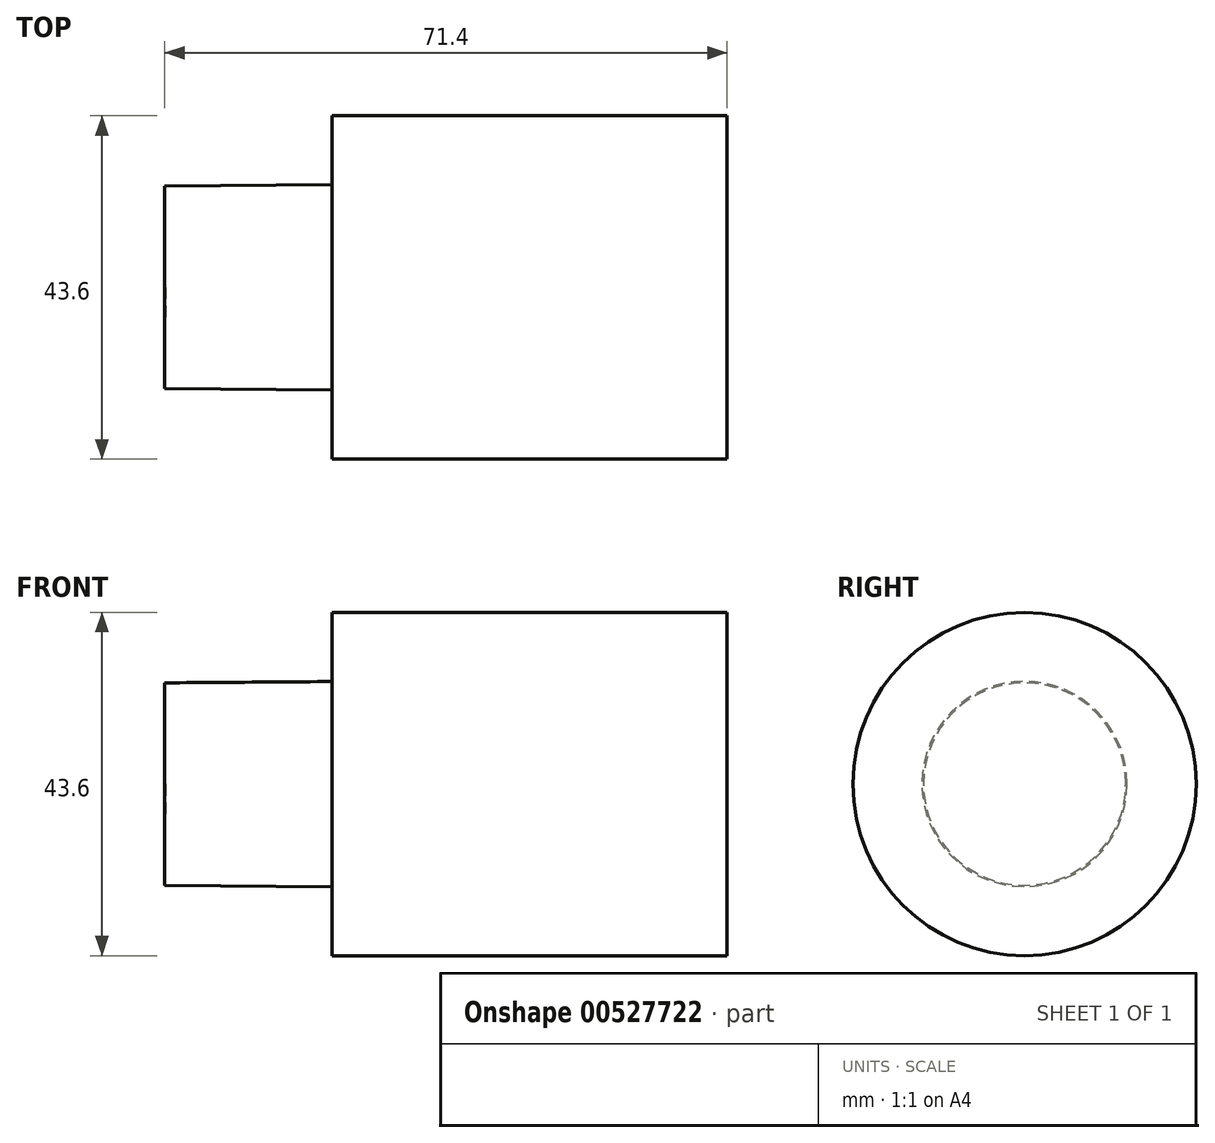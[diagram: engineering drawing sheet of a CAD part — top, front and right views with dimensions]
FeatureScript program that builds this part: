
annotation { "Feature Type Name" : "Feature", "Feature Type Description" : "" }
export const myFeature = defineFeature(function(context is Context, id is Id, definition is map)
    precondition{}
    {
        {
            var Q0;
            Q0=qCreatedBy(makeId("Front.planeOp"),FACE);
            var sketch = newSketch(context, id + "F0", { "sketchPlane" : qUnion([Q0])});
            skLineSegment(sketch, "E0", {"start": v(-50.18, 21.8) * mm, "end": v(0, 21.8) * mm});
            skLineSegment(sketch, "E1", {"start": v(0, 21.8) * mm, "end": v(0, 0) * mm});
            skLineSegment(sketch, "E2", {"start": v(0, 0) * mm, "end": v(-50, 0) * mm});
            skLineSegment(sketch, "E3", {"start": v(-50.11, 13.03) * mm, "end": v(-50.18, 21.8) * mm});
            skLineSegment(sketch, "E4", {"start": v(-50.11, 13.03) * mm, "end": v(-71.4, 12.86) * mm});
            skLineSegment(sketch, "E5", {"start": v(-71.4, 12.86) * mm, "end": v(-71.3, 0) * mm});
            skLineSegment(sketch, "E6", {"start": v(-71.3, 0) * mm, "end": v(-50, 0) * mm});
            skSolve(sketch);
        }
        {
            var Q0;
            Q0=makeQuery(id+"F0.imprint","IMPRINT",FACE,{"disambiguationData":[TD([[makeQuery(id+"F0.imprint","IMPRINT",EDGE,{"derivedFrom":sQuery(id+"F0.wireOp",EDGE,"E0")}),-1.0]])]});
            var Q1;
            Q1=sQuery(id+"F0.wireOp",EDGE,"E6");
            revolve(context, id + "F1", {"entities" : qUnion([Q0]), "axis" : qUnion([Q1]), "revolveType" : RevolveType.FULL});
        }
    });
